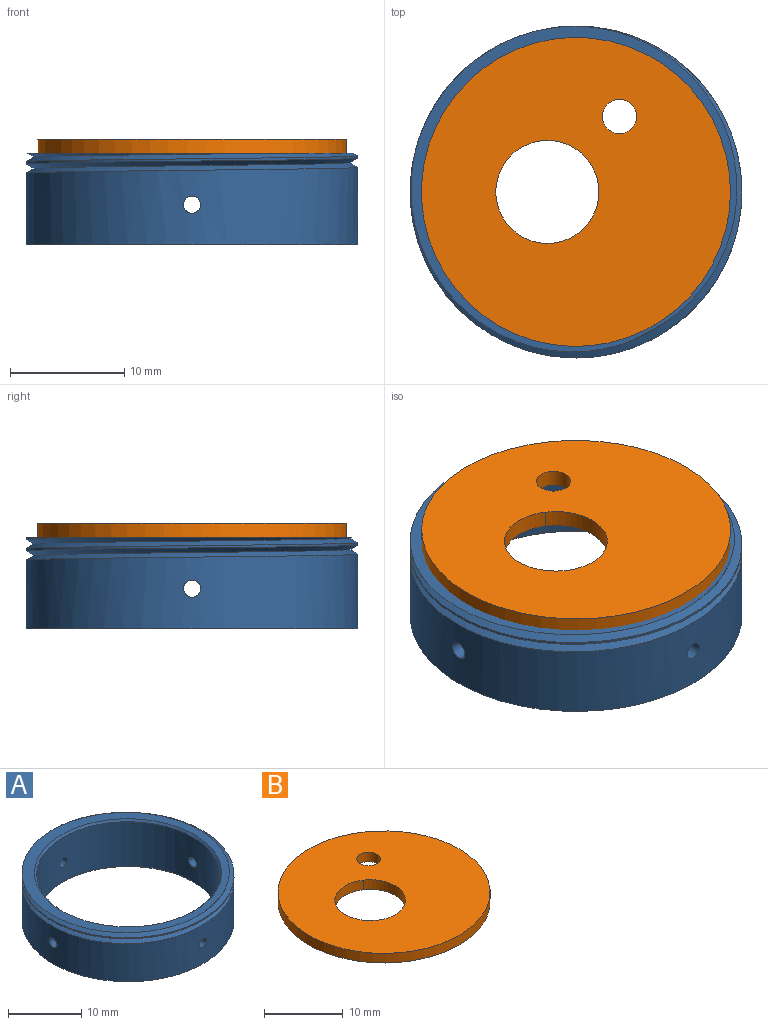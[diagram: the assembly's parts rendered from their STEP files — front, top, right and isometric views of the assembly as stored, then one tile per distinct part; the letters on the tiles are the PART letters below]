
ASSEMBLY  parts=2 mates=1
PART A: 15 faces, bbox 29.5x34x9.1 mm
  f0: cylinder r=14.5mm len=29mm, axis (0,0,-1), area 562.3mm2, adj f1,f5,f6,f7,f11,f12,f13,f14
  f1: cylinder r=14.5mm len=29mm, axis (0,0,-1), area 18.2mm2, adj f0,f2,f7,f8
  f2: cylinder r=14.5mm len=28.25mm, axis (0,0,-1), area 6.4mm2, adj f1,f4,f7,f8
  f3: cylinder r=12.5mm len=25mm, axis (0,0,-1), area 574.1mm2, adj f9,f10,f11,f12,f13,f14
  f4: plane 29.02x29.02mm, normal (0,0,1), area 121mm2, adj f2,f7,f8,f9
  f5: plane 29x29mm, normal (0,0,-1), area 145.8mm2, adj f0,f10
  f6: plane 0.8x0.69mm, normal (0,1,0), area 0.3mm2, adj f0,f7,f8
  f7: bspline ~33.49x29mm, area 146mm2, adj f0,f1,f2,f4,f6,f8
  f8: bspline ~33.49x29mm, area 117.3mm2, adj f1,f2,f4,f6,f7
  f9: cone r=12.5mm half-angle=45deg, axis (0,0,1), area 33.7mm2, adj f3,f4
  f10: cone r=12.8mm half-angle=45deg, axis (0,0,-1), area 33.7mm2, adj f3,f5
  f11: cylinder r=0.75mm len=2mm, axis (0,-1,0), area 9.4mm2, adj f0,f3
  f12: cylinder r=0.75mm len=2mm, axis (0,-1,0), area 9.4mm2, adj f0,f3
  f13: cylinder r=0.75mm len=2mm, axis (1,0,0), area 9.4mm2, adj f0,f3
  f14: cylinder r=0.75mm len=2mm, axis (1,0,0), area 9.4mm2, adj f0,f3
PART B: 10 faces, bbox 27x27x1.5 mm
  f0: cylinder r=3.75mm len=1.5mm, axis (0,0,-1), area 0mm2, adj f1,f6,f7,f8
  f1: cylinder r=4.5mm len=9mm, axis (0,0,-1), area 29.1mm2, adj f0,f2,f7,f8
  f2: cylinder r=3.75mm len=1.5mm, axis (0,0,-1), area 0mm2, adj f1,f3,f7,f8
  f3: plane 1.5x0.01mm, normal (-1,0,0), area 0mm2, adj f2,f4,f7,f8
  f4: cylinder r=4.5mm len=7.48mm, axis (0,0,-1), area 13.3mm2, adj f3,f6,f7,f8
  f5: cylinder r=13.5mm len=27mm, axis (0,0,-1), area 127.2mm2, adj f7,f8
  f6: plane 1.5x0.01mm, normal (-1,0,0), area 0mm2, adj f0,f4,f7,f8
  f7: plane 27x27mm, normal (0,0,1), area 501.9mm2, adj f0,f1,f2,f3,f4,f5,f6,f9
  f8: plane 27x27mm, normal (0,0,-1), area 501.9mm2, adj f0,f1,f2,f3,f4,f5,f6,f9
  f9: cylinder r=1.5mm len=3mm, axis (0,0,-1), area 14.1mm2, adj f7,f8
PLACE A t=(57.88,-18.49,-10.45)mm
PLACE B t=(56.61,-19.34,-2.75)mm
MATE fastened A.f3 <-> B.f0  axis (0,0,1) through (57.88,-18.49,-2.75)mm
